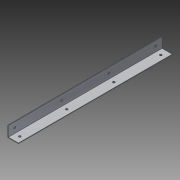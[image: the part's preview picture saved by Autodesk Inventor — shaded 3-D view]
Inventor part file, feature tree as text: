
AUTODESK INVENTOR PART (.ipt)
format: ipt  version: 2014 SP1 (Build 180222100, 222)  size: 104,960 bytes
history: native  units: in
note: dims shown in document units (in); Inventor stores cm internally (conversion verified against a paired STEP export)
features: extrude x3, sketch x3
ambient origin geometry x8: Origin, YZ Plane, XZ Plane, XY Plane, X Axis, Y Axis, Z Axis, Center Point
bodies: Solid1 (feature_tree)
feature tree (6):
  extrude  "Extrusion1"  Depth=0.0312in
  sketch  "Sketch2"  dims[d2=9.0in d3=0.0in d4=0.375in]
  sketch  "Sketch3"  dims[d5=0.125in d6=9.0in d7=1.5748in d9=2.75in d10=0.3937in d12=1.0in d14=0.125in d15=0.375in d16=9.0in d17=1.5748in d19=2.75in d20=0.3937in d22=1.0in d24=1.0in d25=0.0in d26=1.0in d27=0.0in]
  extrude  "Extrusion2"  Depth=9.0in
  extrude  "Extrusion3"  Depth=9.0in
  sketch  "Sketch1"  dims[d0=0.625in d1=0.0312in]
